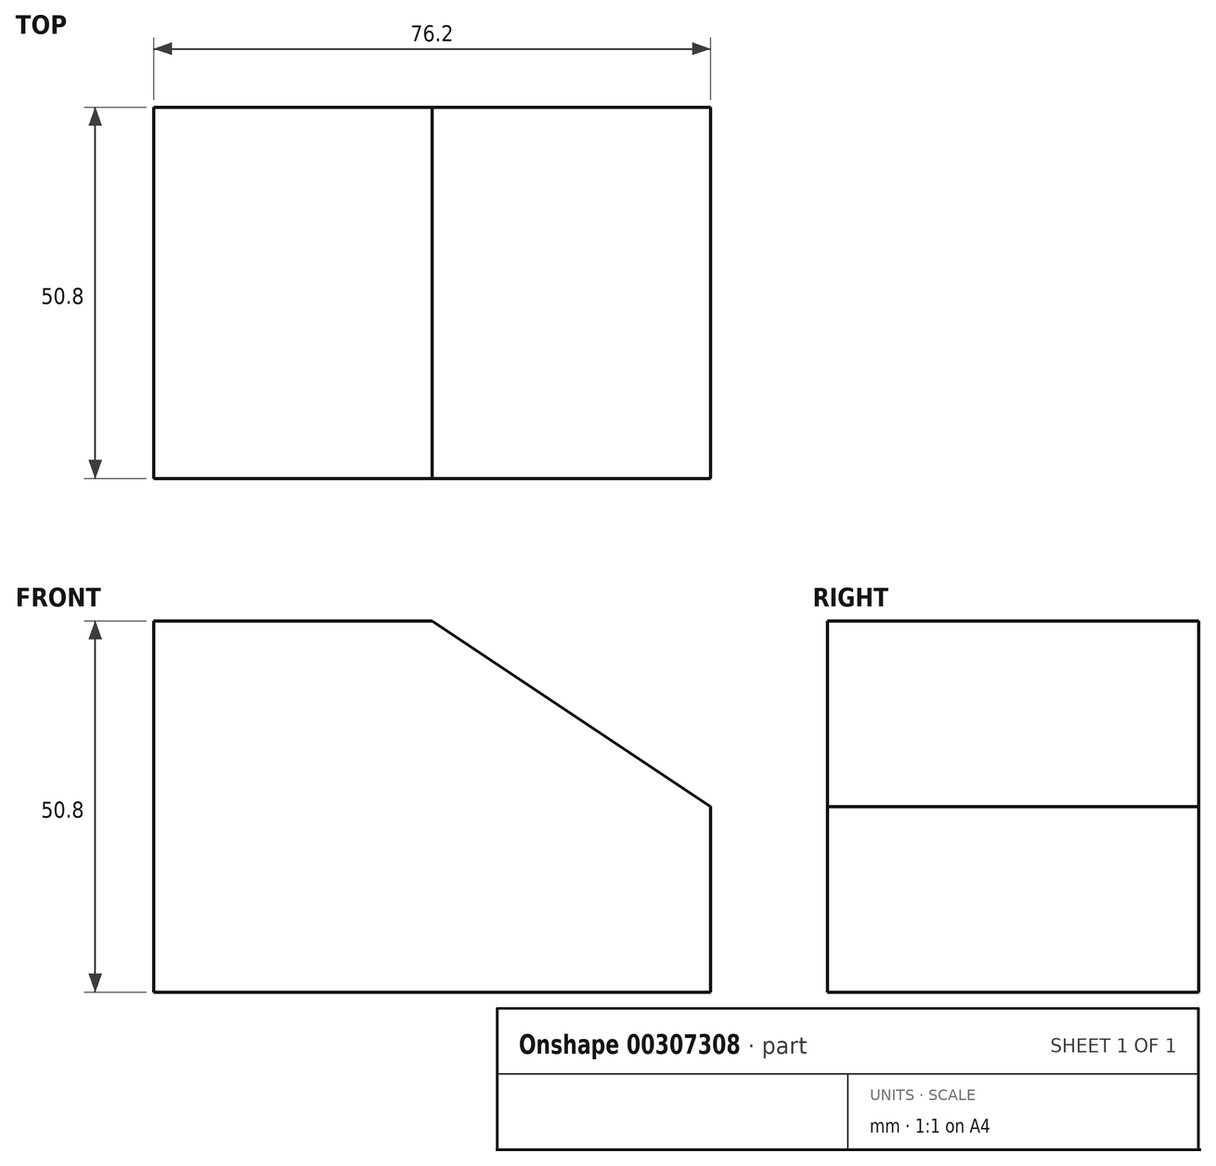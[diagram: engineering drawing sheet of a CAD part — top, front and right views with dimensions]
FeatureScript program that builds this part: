
annotation { "Feature Type Name" : "Feature", "Feature Type Description" : "" }
export const myFeature = defineFeature(function(context is Context, id is Id, definition is map)
    precondition{}
    {
        {
            var Q0;
            Q0=qCreatedBy(makeId("Front.planeOp"),FACE);
            var sketch = newSketch(context, id + "F0", { "sketchPlane" : qUnion([Q0])});
            skLineSegment(sketch, "E0", {"start": v(-41.7, 21.62) * mm, "end": v(-41.7, -29.18) * mm});
            skLineSegment(sketch, "E1", {"start": v(-41.7, -29.18) * mm, "end": v(34.5, -29.18) * mm});
            skLineSegment(sketch, "E2", {"start": v(34.5, -29.18) * mm, "end": v(34.5, -3.78) * mm});
            skLineSegment(sketch, "E3", {"start": v(34.5, -3.78) * mm, "end": v(-3.6, 21.62) * mm});
            skLineSegment(sketch, "E4", {"start": v(-3.6, 21.62) * mm, "end": v(-41.7, 21.62) * mm});
            skSolve(sketch);
        }
        {
            var Q0;
            Q0=makeQuery(id+"F0.imprint","IMPRINT",FACE,{"disambiguationData":[TD([[makeQuery(id+"F0.imprint","IMPRINT",EDGE,{"derivedFrom":sQuery(id+"F0.wireOp",EDGE,"E0")}),1.0]])]});
            extrude(context, id + "F1", {"entities" : qUnion([Q0]), "depth" : 50.8 * mm});
        }
    });
